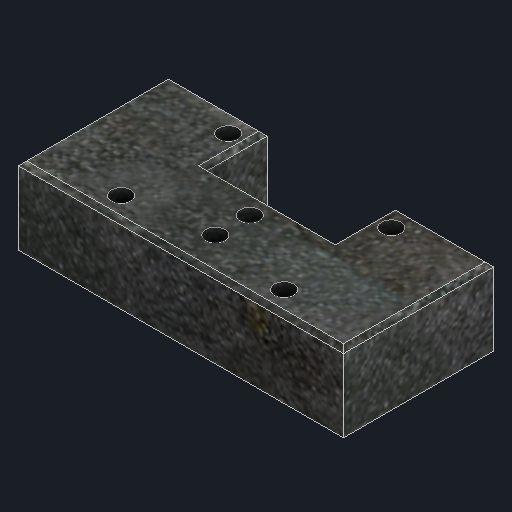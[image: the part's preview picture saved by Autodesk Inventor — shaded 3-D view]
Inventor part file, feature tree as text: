
AUTODESK INVENTOR PART (.ipt)
format: ipt  version: 2023 (Build 270158000, 158)  size: 304,640 bytes
history: native  units: mm
features: extrude x1, chamfer x1, sketch x1
ambient origin geometry x8: Origin, YZ Plane, XZ Plane, XY Plane, X Axis, Y Axis, Z Axis, Center Point
bodies: Solid1 (feature_tree)
feature tree (3):
  extrude  "Extrusion1"  Depth=35.0mm
  chamfer  "Chamfer1"  Distance=23.0mm
  sketch  "Sketch1"  dims[d0=75.8mm d1=35.0mm d2=23.0mm d3=14.0mm d4=29.9mm d7=4.5mm d8=4.5mm d11=4.5mm d12=4.5mm d13=18.0mm d14=0.0mm d15=1.0mm d16=2.0mm d17=45.0deg d20=38.0mm d21=0.0mm d23=38.0mm]
